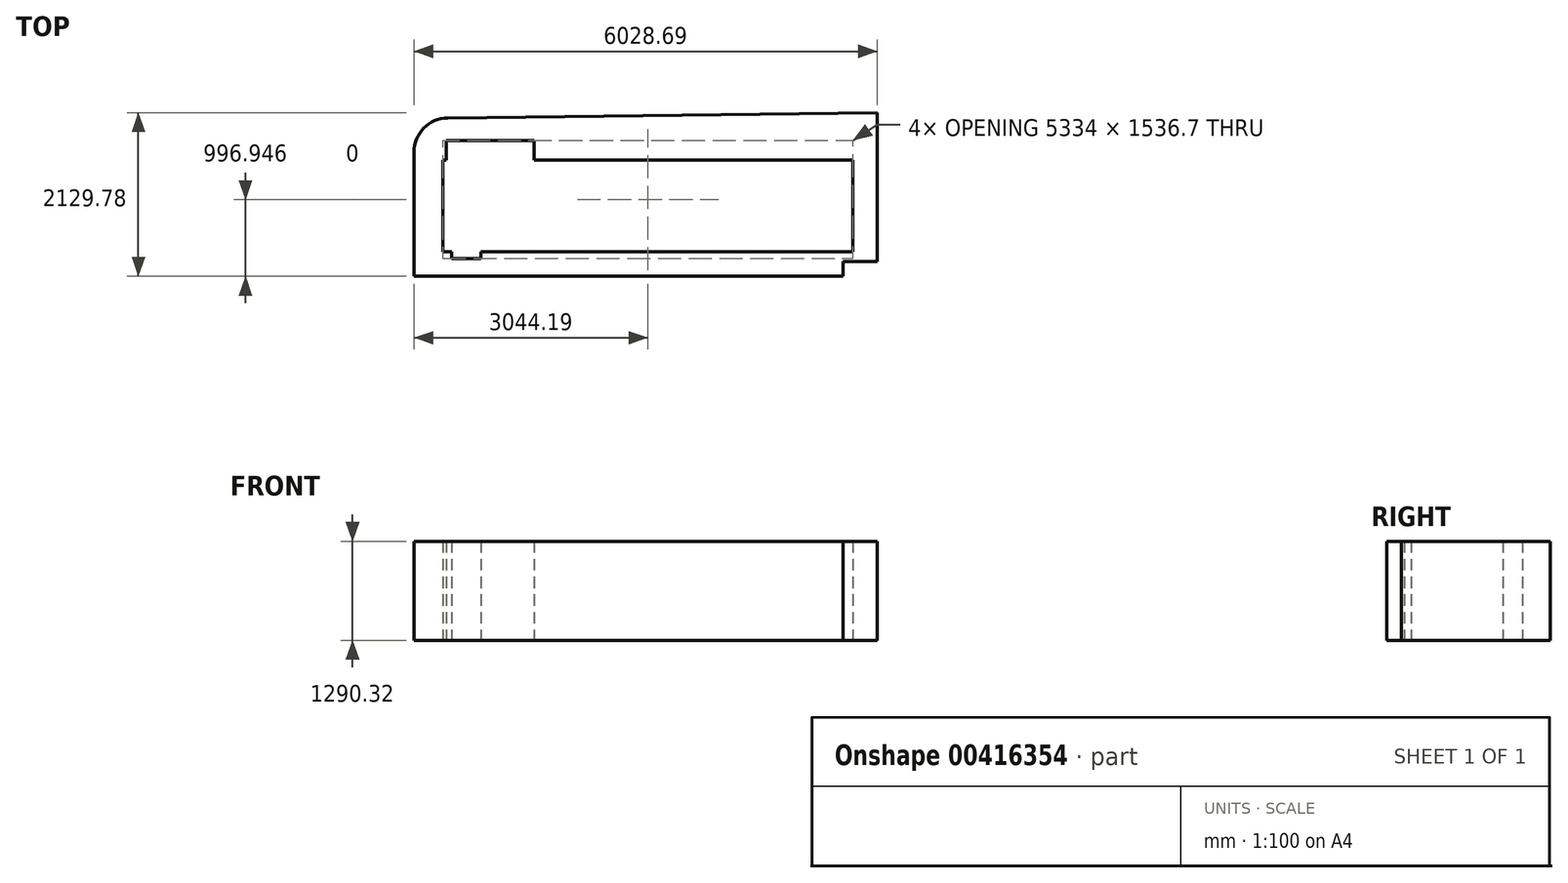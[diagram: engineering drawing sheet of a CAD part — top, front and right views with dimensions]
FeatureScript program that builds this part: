
annotation { "Feature Type Name" : "Feature", "Feature Type Description" : "" }
export const myFeature = defineFeature(function(context is Context, id is Id, definition is map)
    precondition{}
    {
        {
            var Q0;
            Q0=qCreatedBy(makeId("Top.planeOp"),FACE);
            var sketch = newSketch(context, id + "F0", { "sketchPlane" : qUnion([Q0])});
            skLineSegment(sketch, "E0.bottom", {"start": v(3103.21, 1203.02) * mm, "end": v(-2925.48, 1203.02) * mm});
            skLineSegment(sketch, "E0.top", {"start": v(3103.21, -853.11) * mm, "end": v(-2925.48, -853.11) * mm});
            skLineSegment(sketch, "E0.left", {"start": v(3103.21, 1203.02) * mm, "end": v(3103.21, -853.11) * mm});
            skLineSegment(sketch, "E0.right", {"start": v(-2925.48, 1203.02) * mm, "end": v(-2925.48, -853.11) * mm});
            skPoint(sketch, "E0.middle", {"position": v(88.87, 174.95) * mm});
            skLineSegment(sketch, "E1", {"start": v(-2925.48, 1203.02) * mm, "end": v(3103.21, 1276.67) * mm});
            skLineSegment(sketch, "E2", {"start": v(3103.21, 1276.67) * mm, "end": v(3103.21, 1203.02) * mm});
            skLineSegment(sketch, "E3.bottom", {"start": v(-2548.29, -535.61) * mm, "end": v(2785.71, -535.61) * mm});
            skLineSegment(sketch, "E3.top", {"start": v(-2548.29, 658.19) * mm, "end": v(2785.71, 658.19) * mm});
            skLineSegment(sketch, "E3.left", {"start": v(-2548.29, -535.61) * mm, "end": v(-2548.29, 658.19) * mm});
            skLineSegment(sketch, "E3.right", {"start": v(2785.71, -535.61) * mm, "end": v(2785.71, 658.19) * mm});
            skLineSegment(sketch, "E4.bottom", {"start": v(3103.21, -853.11) * mm, "end": v(2658.71, -853.11) * mm});
            skLineSegment(sketch, "E4.top", {"start": v(3103.21, -662.61) * mm, "end": v(2658.71, -662.61) * mm});
            skLineSegment(sketch, "E4.left", {"start": v(3103.21, -853.11) * mm, "end": v(3103.21, -662.61) * mm});
            skLineSegment(sketch, "E4.right", {"start": v(2658.71, -853.11) * mm, "end": v(2658.71, -662.61) * mm});
            skLineSegment(sketch, "E5.bottom", {"start": v(2785.71, -535.61) * mm, "end": v(-1849.79, -535.61) * mm});
            skLineSegment(sketch, "E5.top", {"start": v(2785.71, -27.61) * mm, "end": v(-1849.79, -27.61) * mm});
            skLineSegment(sketch, "E5.left", {"start": v(2785.71, -535.61) * mm, "end": v(2785.71, -27.61) * mm});
            skLineSegment(sketch, "E5.right", {"start": v(-1849.79, -535.61) * mm, "end": v(-1849.79, -27.61) * mm});
            skLineSegment(sketch, "E6.bottom", {"start": v(-1360.84, 658.19) * mm, "end": v(-2503.84, 658.19) * mm});
            skLineSegment(sketch, "E6.top", {"start": v(-1360.84, 912.19) * mm, "end": v(-2503.84, 912.19) * mm});
            skLineSegment(sketch, "E6.left", {"start": v(-1360.84, 658.19) * mm, "end": v(-1360.84, 912.19) * mm});
            skLineSegment(sketch, "E6.right", {"start": v(-2503.84, 658.19) * mm, "end": v(-2503.84, 912.19) * mm});
            skLineSegment(sketch, "E7.bottom", {"start": v(-2055.78, -535.61) * mm, "end": v(-2436.78, -535.61) * mm});
            skLineSegment(sketch, "E7.top", {"start": v(-2055.78, -624.51) * mm, "end": v(-2436.78, -624.51) * mm});
            skLineSegment(sketch, "E7.left", {"start": v(-2055.78, -535.61) * mm, "end": v(-2055.78, -624.51) * mm});
            skLineSegment(sketch, "E7.right", {"start": v(-2436.78, -535.61) * mm, "end": v(-2436.78, -624.51) * mm});
            skSolve(sketch);
        }
        {
            var Q0;
            Q0=makeQuery(id+"F0.imprint","IMPRINT",FACE,{"disambiguationData":[TD([[makeQuery(id+"F0.imprint","IMPRINT",EDGE,{"derivedFrom":sQuery(id+"F0.wireOp",EDGE,"E0.bottom")}),1.0]])]});
            var Q1;
            Q1=makeQuery(id+"F0.imprint","IMPRINT",FACE,{"disambiguationData":[TD([[makeQuery(id+"F0.imprint","IMPRINT",EDGE,{"derivedFrom":sQuery(id+"F0.wireOp",EDGE,"E0.bottom")}),-1.0]])]});
            extrude(context, id + "F1", {"entities" : qUnion([Q0, Q1]), "depth" : 1290.32 * mm});
        }
        {
            var Q0;
            Q0=makeQuery(id+"F1.opExtrude","SWEPT_EDGE",EDGE,{"disambiguationData":[OSD([sQuery(id+"F0.wireOp",EDGE,"E0.bottom"),sQuery(id+"F0.wireOp",EDGE,"E0.right"),sQuery(id+"F0.wireOp",EDGE,"E1")])]});
            fillet(context, id + "F2", {"entities" : qUnion([Q0]), "radius" : 444 * mm, "tangentPropagation" : true, "allowEdgeOverflow" : false});
        }
    });
